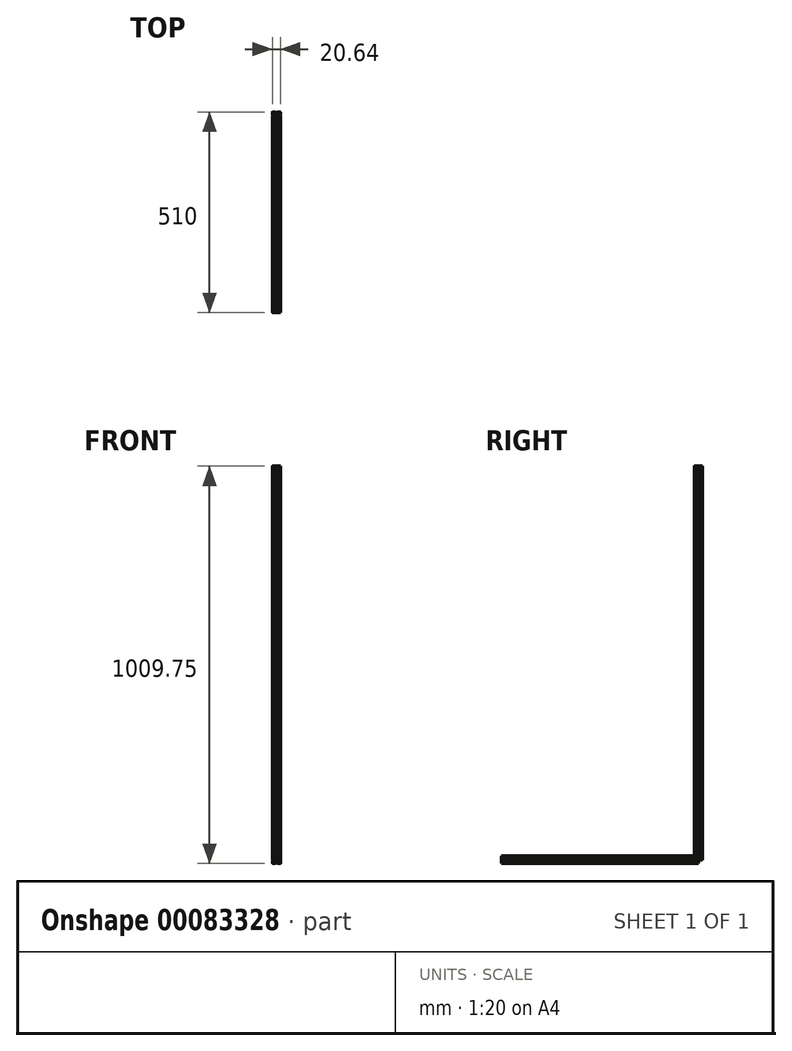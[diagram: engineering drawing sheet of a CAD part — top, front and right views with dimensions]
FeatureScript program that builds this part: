
annotation { "Feature Type Name" : "Feature", "Feature Type Description" : "" }
export const myFeature = defineFeature(function(context is Context, id is Id, definition is map)
    precondition{}
    {
        {
            assignVariable(context, id + "F0", {"name" : "VerticalLength", "anyValue" : 1000});
        }
        {
            var Q0;
            Q0=qCreatedBy(makeId("Top.planeOp"),FACE);
            var sketch = newSketch(context, id + "F1", { "sketchPlane" : qUnion([Q0])});
            skLineSegment(sketch, "E0.top", {"start": v(9.5, -10) * mm, "end": v(3.15, -10) * mm});
            skLineSegment(sketch, "E0.left", {"start": v(10, 9.5) * mm, "end": v(10, 3.15) * mm});
            skPoint(sketch, "E0.middle", {"position": v(0, 0) * mm});
            skLineSegment(sketch, "E1", {"start": v(-10, 0) * mm, "end": v(10, 0) * mm, "construction": true});
            skLineSegment(sketch, "E2", {"start": v(0, 10) * mm, "end": v(0, -10) * mm, "construction": true});
            skPoint(sketch, "E3.visualSharp", {"position": v(-10, 10) * mm});
            skPoint(sketch, "E4", {"position": v(-10, 2.65) * mm});
            skPoint(sketch, "E5.visualSharp", {"position": v(-8.5, 2.65) * mm});
            skLineSegment(sketch, "E6", {"start": v(-10, 10) * mm, "end": v(0, 0) * mm, "construction": true});
            skPoint(sketch, "E7.visualSharp", {"position": v(-8.5, 7.44) * mm});
            skLineSegment(sketch, "E8", {"start": v(-7.65, 6.59) * mm, "end": v(-3.76, 2.7) * mm});
            skLineSegment(sketch, "E9", {"start": v(-8.5, 6.23) * mm, "end": v(-8.5, 3.15) * mm});
            skLineSegment(sketch, "E10", {"start": v(-9.5, 2.65) * mm, "end": v(-9, 2.65) * mm});
            skLineSegment(sketch, "E11.bottom", {"start": v(-9.5, 10) * mm, "end": v(-3.15, 10) * mm});
            skLineSegment(sketch, "E11.top", {"start": v(-9.5, -10) * mm, "end": v(-3.15, -10) * mm});
            skLineSegment(sketch, "E11.left", {"start": v(-10, 9.5) * mm, "end": v(-10, 3.15) * mm});
            skLineSegment(sketch, "E12", {"start": v(-3.6, 2.34) * mm, "end": v(-3.6, 0) * mm});
            skLineSegment(sketch, "E13.MirrorCS", {"start": v(-2.65, 9.5) * mm, "end": v(-2.65, 9) * mm});
            skLineSegment(sketch, "E14.MirrorCS", {"start": v(-6.23, 8.5) * mm, "end": v(-3.15, 8.5) * mm});
            skLineSegment(sketch, "E15.MirrorCS", {"start": v(-2.34, 3.6) * mm, "end": v(0, 3.6) * mm});
            skLineSegment(sketch, "E16.MirrorCS", {"start": v(-6.59, 7.65) * mm, "end": v(-2.7, 3.76) * mm});
            skLineSegment(sketch, "E17.MirrorCS", {"start": v(9.5, 2.65) * mm, "end": v(9, 2.65) * mm});
            skLineSegment(sketch, "E18.MirrorCS", {"start": v(8.5, 6.23) * mm, "end": v(8.5, 3.15) * mm});
            skLineSegment(sketch, "E19.MirrorCS", {"start": v(7.65, 6.59) * mm, "end": v(3.76, 2.7) * mm});
            skLineSegment(sketch, "E20.MirrorCS", {"start": v(3.61, 2.34) * mm, "end": v(3.6, 0) * mm});
            skLineSegment(sketch, "E21.MirrorCS", {"start": v(2.34, 3.6) * mm, "end": v(0, 3.6) * mm});
            skLineSegment(sketch, "E22.MirrorCS", {"start": v(6.59, 7.65) * mm, "end": v(2.7, 3.76) * mm});
            skLineSegment(sketch, "E23.MirrorCS", {"start": v(2.65, 9.5) * mm, "end": v(2.65, 9) * mm});
            skLineSegment(sketch, "E24.MirrorCS", {"start": v(6.23, 8.5) * mm, "end": v(3.15, 8.5) * mm});
            skLineSegment(sketch, "E25.MirrorCS", {"start": v(-9.5, -2.65) * mm, "end": v(-8.8, -2.65) * mm});
            skPoint(sketch, "E26.MirrorP", {"position": v(-10, -2.65) * mm});
            skLineSegment(sketch, "E27.MirrorCS", {"start": v(2.65, -9.5) * mm, "end": v(2.65, -9) * mm});
            skLineSegment(sketch, "E28.MirrorCS", {"start": v(8.5, -6.23) * mm, "end": v(8.5, -3.15) * mm});
            skLineSegment(sketch, "E29.MirrorCS", {"start": v(3.61, -2.34) * mm, "end": v(3.6, 0) * mm});
            skLineSegment(sketch, "E30.MirrorCS", {"start": v(-3.6, -2.34) * mm, "end": v(-3.6, 0) * mm});
            skLineSegment(sketch, "E31.MirrorCS", {"start": v(-6.59, -7.65) * mm, "end": v(-2.7, -3.76) * mm});
            skLineSegment(sketch, "E32.MirrorCS", {"start": v(-2.65, -9.5) * mm, "end": v(-2.65, -9) * mm});
            skLineSegment(sketch, "E33.MirrorCS", {"start": v(-6.23, -8.5) * mm, "end": v(-3.15, -8.5) * mm});
            skPoint(sketch, "E34.MirrorP", {"position": v(-8.5, -2.65) * mm});
            skLineSegment(sketch, "E35.MirrorCS", {"start": v(7.65, -6.59) * mm, "end": v(3.76, -2.7) * mm});
            skLineSegment(sketch, "E36.MirrorCS", {"start": v(2.34, -3.6) * mm, "end": v(0, -3.6) * mm});
            skLineSegment(sketch, "E37.MirrorCS", {"start": v(6.59, -7.65) * mm, "end": v(2.7, -3.76) * mm});
            skLineSegment(sketch, "E38.MirrorCS", {"start": v(-8.5, -6.23) * mm, "end": v(-8.5, -2.95) * mm});
            skLineSegment(sketch, "E39.MirrorCS", {"start": v(-7.65, -6.59) * mm, "end": v(-3.76, -2.7) * mm});
            skLineSegment(sketch, "E40.MirrorCS", {"start": v(9.5, -2.65) * mm, "end": v(9, -2.65) * mm});
            skPoint(sketch, "E41.MirrorP", {"position": v(-8.5, -7.44) * mm});
            skPoint(sketch, "E42.MirrorP", {"position": v(-10, -10) * mm});
            skLineSegment(sketch, "E43.MirrorCS", {"start": v(6.23, -8.5) * mm, "end": v(3.15, -8.5) * mm});
            skLineSegment(sketch, "E44.MirrorCS", {"start": v(-2.34, -3.6) * mm, "end": v(0, -3.6) * mm});
            skLineSegment(sketch, "E45.trimOffspring", {"start": v(3.15, 10) * mm, "end": v(9.5, 10) * mm});
            skLineSegment(sketch, "E46.trimOffspring", {"start": v(-10, -3.15) * mm, "end": v(-10, -9.5) * mm});
            skLineSegment(sketch, "E47.trimOffspring", {"start": v(10, -3.15) * mm, "end": v(10, -9.5) * mm});
            skPoint(sketch, "E48.MirrorCS.end.orphan", {"position": v(-10, 0) * mm});
            skLineSegment(sketch, "E49.trimOffspring", {"start": v(3.15, -10) * mm, "end": v(9.5, -10) * mm});
            skLineSegment(sketch, "E50.trimOffspring", {"start": v(-3.15, -10) * mm, "end": v(-9.5, -10) * mm});
            skArc(sketch, "E51.filletArc", {"start": v(-10, 3.15) * mm, "mid": v(-9.85, 2.8) * mm, "end": v(-9.5, 2.65) * mm});
            skArc(sketch, "E52.filletArc", {"start": v(-9, 2.65) * mm, "mid": v(-8.65, 2.8) * mm, "end": v(-8.5, 3.15) * mm});
            skArc(sketch, "E53.filletArc", {"start": v(-9.5, -2.65) * mm, "mid": v(-9.85, -2.8) * mm, "end": v(-10, -3.15) * mm});
            skArc(sketch, "E54.filletArc", {"start": v(-8.5, -2.95) * mm, "mid": v(-8.59, -2.74) * mm, "end": v(-8.8, -2.65) * mm});
            skArc(sketch, "E55.filletArc", {"start": v(-9.5, 10) * mm, "mid": v(-9.85, 9.85) * mm, "end": v(-10, 9.5) * mm});
            skPoint(sketch, "E56.visualSharp", {"position": v(-2.65, 10) * mm});
            skArc(sketch, "E56.filletArc", {"start": v(-2.65, 9.5) * mm, "mid": v(-2.8, 9.85) * mm, "end": v(-3.15, 10) * mm});
            skPoint(sketch, "E57.visualSharp", {"position": v(-2.65, 8.5) * mm});
            skArc(sketch, "E57.filletArc", {"start": v(-3.15, 8.5) * mm, "mid": v(-2.8, 8.65) * mm, "end": v(-2.65, 9) * mm});
            skArc(sketch, "E58.filletArc", {"start": v(-7.65, 6.59) * mm, "mid": v(-8.2, 6.7) * mm, "end": v(-8.5, 6.23) * mm});
            skPoint(sketch, "E59.visualSharp", {"position": v(-7.44, 8.5) * mm});
            skArc(sketch, "E59.filletArc", {"start": v(-6.23, 8.5) * mm, "mid": v(-6.7, 8.2) * mm, "end": v(-6.59, 7.65) * mm});
            skPoint(sketch, "E60.visualSharp", {"position": v(-2.55, 3.6) * mm});
            skArc(sketch, "E60.filletArc", {"start": v(-2.7, 3.76) * mm, "mid": v(-2.53, 3.65) * mm, "end": v(-2.34, 3.61) * mm});
            skPoint(sketch, "E61.visualSharp", {"position": v(2.55, 3.6) * mm});
            skArc(sketch, "E61.filletArc", {"start": v(2.34, 3.6) * mm, "mid": v(2.53, 3.65) * mm, "end": v(2.7, 3.76) * mm});
            skPoint(sketch, "E62.visualSharp", {"position": v(7.44, 8.5) * mm});
            skArc(sketch, "E62.filletArc", {"start": v(6.59, 7.65) * mm, "mid": v(6.7, 8.2) * mm, "end": v(6.23, 8.5) * mm});
            skPoint(sketch, "E63.visualSharp", {"position": v(2.65, 8.5) * mm});
            skArc(sketch, "E63.filletArc", {"start": v(2.65, 9) * mm, "mid": v(2.8, 8.65) * mm, "end": v(3.15, 8.5) * mm});
            skPoint(sketch, "E64.visualSharp", {"position": v(2.65, 10) * mm});
            skArc(sketch, "E64.filletArc", {"start": v(3.15, 10) * mm, "mid": v(2.8, 9.85) * mm, "end": v(2.65, 9.5) * mm});
            skArc(sketch, "E65.filletArc", {"start": v(-10, -9.5) * mm, "mid": v(-9.85, -9.85) * mm, "end": v(-9.5, -10) * mm});
            skPoint(sketch, "E66.visualSharp", {"position": v(10, -10) * mm});
            skArc(sketch, "E66.filletArc", {"start": v(9.5, -10) * mm, "mid": v(9.85, -9.85) * mm, "end": v(10, -9.5) * mm});
            skPoint(sketch, "E67.visualSharp", {"position": v(-2.65, -8.5) * mm});
            skArc(sketch, "E67.filletArc", {"start": v(-2.65, -9) * mm, "mid": v(-2.8, -8.65) * mm, "end": v(-3.15, -8.5) * mm});
            skPoint(sketch, "E68.visualSharp", {"position": v(2.65, -8.5) * mm});
            skArc(sketch, "E68.filletArc", {"start": v(3.15, -8.5) * mm, "mid": v(2.8, -8.65) * mm, "end": v(2.65, -9) * mm});
            skPoint(sketch, "E69.visualSharp", {"position": v(-2.55, -3.61) * mm});
            skArc(sketch, "E69.filletArc", {"start": v(-2.34, -3.6) * mm, "mid": v(-2.53, -3.65) * mm, "end": v(-2.7, -3.76) * mm});
            skPoint(sketch, "E70.visualSharp", {"position": v(2.55, -3.6) * mm});
            skArc(sketch, "E70.filletArc", {"start": v(2.7, -3.76) * mm, "mid": v(2.53, -3.65) * mm, "end": v(2.34, -3.6) * mm});
            skPoint(sketch, "E71.visualSharp", {"position": v(7.44, -8.5) * mm});
            skArc(sketch, "E71.filletArc", {"start": v(6.23, -8.5) * mm, "mid": v(6.7, -8.2) * mm, "end": v(6.59, -7.65) * mm});
            skPoint(sketch, "E72.visualSharp", {"position": v(-7.44, -8.5) * mm});
            skArc(sketch, "E72.filletArc", {"start": v(-6.59, -7.65) * mm, "mid": v(-6.7, -8.2) * mm, "end": v(-6.23, -8.5) * mm});
            skArc(sketch, "E73.filletArc", {"start": v(-8.5, -6.23) * mm, "mid": v(-8.2, -6.7) * mm, "end": v(-7.65, -6.59) * mm});
            skPoint(sketch, "E74.visualSharp", {"position": v(-3.6, 2.55) * mm});
            skArc(sketch, "E74.filletArc", {"start": v(-3.6, 2.34) * mm, "mid": v(-3.65, 2.53) * mm, "end": v(-3.76, 2.7) * mm});
            skPoint(sketch, "E75.visualSharp", {"position": v(-3.6, -2.55) * mm});
            skArc(sketch, "E75.filletArc", {"start": v(-3.76, -2.7) * mm, "mid": v(-3.65, -2.53) * mm, "end": v(-3.6, -2.34) * mm});
            skPoint(sketch, "E76.visualSharp", {"position": v(3.6, 2.55) * mm});
            skArc(sketch, "E76.filletArc", {"start": v(3.76, 2.7) * mm, "mid": v(3.65, 2.53) * mm, "end": v(3.61, 2.34) * mm});
            skPoint(sketch, "E77.visualSharp", {"position": v(3.61, -2.55) * mm});
            skArc(sketch, "E77.filletArc", {"start": v(3.61, -2.34) * mm, "mid": v(3.65, -2.53) * mm, "end": v(3.76, -2.7) * mm});
            skPoint(sketch, "E78.visualSharp", {"position": v(8.5, -7.44) * mm});
            skArc(sketch, "E78.filletArc", {"start": v(7.65, -6.59) * mm, "mid": v(8.2, -6.7) * mm, "end": v(8.5, -6.23) * mm});
            skPoint(sketch, "E79.visualSharp", {"position": v(8.5, -2.65) * mm});
            skArc(sketch, "E79.filletArc", {"start": v(9, -2.65) * mm, "mid": v(8.65, -2.8) * mm, "end": v(8.5, -3.15) * mm});
            skPoint(sketch, "E80.visualSharp", {"position": v(10, -2.65) * mm});
            skArc(sketch, "E80.filletArc", {"start": v(10, -3.15) * mm, "mid": v(9.85, -2.8) * mm, "end": v(9.5, -2.65) * mm});
            skPoint(sketch, "E81.visualSharp", {"position": v(-2.65, -10) * mm});
            skArc(sketch, "E81.filletArc", {"start": v(-3.15, -10) * mm, "mid": v(-2.8, -9.85) * mm, "end": v(-2.65, -9.5) * mm});
            skPoint(sketch, "E82.visualSharp", {"position": v(2.65, -10) * mm});
            skArc(sketch, "E82.filletArc", {"start": v(2.65, -9.5) * mm, "mid": v(2.8, -9.85) * mm, "end": v(3.15, -10) * mm});
            skPoint(sketch, "E83.visualSharp", {"position": v(8.5, 7.44) * mm});
            skArc(sketch, "E83.filletArc", {"start": v(8.5, 6.23) * mm, "mid": v(8.2, 6.7) * mm, "end": v(7.65, 6.59) * mm});
            skPoint(sketch, "E84.visualSharp", {"position": v(8.5, 2.65) * mm});
            skArc(sketch, "E84.filletArc", {"start": v(8.5, 3.15) * mm, "mid": v(8.65, 2.8) * mm, "end": v(9, 2.65) * mm});
            skPoint(sketch, "E85.visualSharp", {"position": v(10, 10) * mm});
            skArc(sketch, "E85.filletArc", {"start": v(10, 9.5) * mm, "mid": v(9.85, 9.85) * mm, "end": v(9.5, 10) * mm});
            skPoint(sketch, "E86.visualSharp", {"position": v(10, 2.65) * mm});
            skArc(sketch, "E86.filletArc", {"start": v(9.5, 2.65) * mm, "mid": v(9.85, 2.8) * mm, "end": v(10, 3.15) * mm});
            skSolve(sketch);
        }
        {
            var Q0;
            Q0=makeQuery(id+"F1.imprint","IMPRINT",FACE,{"disambiguationData":[TD([[makeQuery(id+"F1.imprint","IMPRINT",EDGE,{"derivedFrom":sQuery(id+"F1.wireOp",EDGE,"E8")}),1.0]])]});
            extrude(context, id + "F2", {"entities" : qUnion([Q0]), "depth" : (getVariable(context, 'VerticalLength')) * mm});
        }
        {
            assignVariable(context, id + "F3", {"name" : "HorizontalLength", "anyValue" : 500});
        }
        {
            var Q0;
            Q0=qCreatedBy(makeId("Front.planeOp"),FACE);
            var sketch = newSketch(context, id + "F4", { "sketchPlane" : qUnion([Q0])});
            skLineSegment(sketch, "E87.top", {"start": v(10.14, -9.75) * mm, "end": v(3.8, -9.75) * mm});
            skLineSegment(sketch, "E87.left", {"start": v(10.64, 9.75) * mm, "end": v(10.64, 3.4) * mm});
            skPoint(sketch, "E87.middle", {"position": v(0.64, 0.25) * mm});
            skLineSegment(sketch, "E88", {"start": v(-9.36, 0.25) * mm, "end": v(10.64, 0.25) * mm, "construction": true});
            skLineSegment(sketch, "E89", {"start": v(0.64, 10.25) * mm, "end": v(0.64, -9.75) * mm, "construction": true});
            skPoint(sketch, "E90.visualSharp", {"position": v(-9.36, 10.25) * mm});
            skPoint(sketch, "E91", {"position": v(-9.36, 2.9) * mm});
            skPoint(sketch, "E92.visualSharp", {"position": v(-7.86, 2.9) * mm});
            skLineSegment(sketch, "E93", {"start": v(-9.36, 10.25) * mm, "end": v(0.64, 0.25) * mm, "construction": true});
            skPoint(sketch, "E94.visualSharp", {"position": v(-7.86, 7.7) * mm});
            skLineSegment(sketch, "E95", {"start": v(-7, 6.84) * mm, "end": v(-3.11, 2.95) * mm});
            skLineSegment(sketch, "E96", {"start": v(-7.86, 6.48) * mm, "end": v(-7.86, 3.4) * mm});
            skLineSegment(sketch, "E97", {"start": v(-8.86, 2.9) * mm, "end": v(-8.36, 2.9) * mm});
            skLineSegment(sketch, "E98.bottom", {"start": v(-8.86, 10.25) * mm, "end": v(-2.5, 10.25) * mm});
            skLineSegment(sketch, "E98.top", {"start": v(-8.86, -9.75) * mm, "end": v(-2.5, -9.75) * mm});
            skLineSegment(sketch, "E98.left", {"start": v(-9.36, 9.75) * mm, "end": v(-9.36, 3.4) * mm});
            skLineSegment(sketch, "E99", {"start": v(-2.97, 2.6) * mm, "end": v(-2.97, 0.25) * mm});
            skLineSegment(sketch, "E100.MirrorCS", {"start": v(-2, 9.75) * mm, "end": v(-2, 9.25) * mm});
            skLineSegment(sketch, "E101.MirrorCS", {"start": v(-5.59, 8.75) * mm, "end": v(-2.5, 8.75) * mm});
            skLineSegment(sketch, "E102.MirrorCS", {"start": v(-1.7, 3.86) * mm, "end": v(0.64, 3.86) * mm});
            skLineSegment(sketch, "E103.MirrorCS", {"start": v(-5.94, 7.9) * mm, "end": v(-2.05, 4) * mm});
            skLineSegment(sketch, "E104.MirrorCS", {"start": v(10.14, 2.9) * mm, "end": v(9.64, 2.9) * mm});
            skLineSegment(sketch, "E105.MirrorCS", {"start": v(9.14, 6.48) * mm, "end": v(9.14, 3.4) * mm});
            skLineSegment(sketch, "E106.MirrorCS", {"start": v(8.3, 6.84) * mm, "end": v(4.4, 2.95) * mm});
            skLineSegment(sketch, "E107.MirrorCS", {"start": v(4.25, 2.6) * mm, "end": v(4.25, 0.25) * mm});
            skLineSegment(sketch, "E108.MirrorCS", {"start": v(2.99, 3.86) * mm, "end": v(0.64, 3.86) * mm});
            skLineSegment(sketch, "E109.MirrorCS", {"start": v(7.23, 7.9) * mm, "end": v(3.34, 4) * mm});
            skLineSegment(sketch, "E110.MirrorCS", {"start": v(3.3, 9.75) * mm, "end": v(3.3, 9.25) * mm});
            skLineSegment(sketch, "E111.MirrorCS", {"start": v(6.88, 8.75) * mm, "end": v(3.8, 8.75) * mm});
            skLineSegment(sketch, "E112.MirrorCS", {"start": v(-8.86, -2.4) * mm, "end": v(-8.16, -2.4) * mm});
            skPoint(sketch, "E113.MirrorP", {"position": v(-9.36, -2.4) * mm});
            skLineSegment(sketch, "E114.MirrorCS", {"start": v(3.3, -9.25) * mm, "end": v(3.3, -8.75) * mm});
            skLineSegment(sketch, "E115.MirrorCS", {"start": v(9.14, -5.98) * mm, "end": v(9.14, -2.9) * mm});
            skLineSegment(sketch, "E116.MirrorCS", {"start": v(4.25, -2.09) * mm, "end": v(4.25, 0.25) * mm});
            skLineSegment(sketch, "E117.MirrorCS", {"start": v(-2.97, -2.09) * mm, "end": v(-2.97, 0.25) * mm});
            skLineSegment(sketch, "E118.MirrorCS", {"start": v(-5.94, -7.4) * mm, "end": v(-2.05, -3.5) * mm});
            skLineSegment(sketch, "E119.MirrorCS", {"start": v(-2, -9.25) * mm, "end": v(-2, -8.75) * mm});
            skLineSegment(sketch, "E120.MirrorCS", {"start": v(-5.59, -8.25) * mm, "end": v(-2.5, -8.25) * mm});
            skPoint(sketch, "E121.MirrorP", {"position": v(-7.86, -2.4) * mm});
            skLineSegment(sketch, "E122.MirrorCS", {"start": v(8.3, -6.33) * mm, "end": v(4.4, -2.44) * mm});
            skLineSegment(sketch, "E123.MirrorCS", {"start": v(2.99, -3.36) * mm, "end": v(0.64, -3.36) * mm});
            skLineSegment(sketch, "E124.MirrorCS", {"start": v(7.23, -7.4) * mm, "end": v(3.34, -3.5) * mm});
            skLineSegment(sketch, "E125.MirrorCS", {"start": v(-7.86, -5.98) * mm, "end": v(-7.86, -2.7) * mm});
            skLineSegment(sketch, "E126.MirrorCS", {"start": v(-7, -6.33) * mm, "end": v(-3.11, -2.44) * mm});
            skLineSegment(sketch, "E127.MirrorCS", {"start": v(10.14, -2.4) * mm, "end": v(9.64, -2.4) * mm});
            skPoint(sketch, "E128.MirrorP", {"position": v(-7.86, -7.19) * mm});
            skPoint(sketch, "E129.MirrorP", {"position": v(-9.36, -9.75) * mm});
            skLineSegment(sketch, "E130.MirrorCS", {"start": v(6.88, -8.25) * mm, "end": v(3.8, -8.25) * mm});
            skLineSegment(sketch, "E131.MirrorCS", {"start": v(-1.7, -3.36) * mm, "end": v(0.64, -3.36) * mm});
            skLineSegment(sketch, "E132.trimOffspring", {"start": v(3.8, 10.25) * mm, "end": v(10.14, 10.25) * mm});
            skLineSegment(sketch, "E133.trimOffspring", {"start": v(-9.36, -2.9) * mm, "end": v(-9.36, -9.25) * mm});
            skLineSegment(sketch, "E134.trimOffspring", {"start": v(10.64, -2.9) * mm, "end": v(10.64, -9.25) * mm});
            skPoint(sketch, "E135.MirrorCS.end.orphan", {"position": v(-9.36, 0.25) * mm});
            skLineSegment(sketch, "E136.trimOffspring", {"start": v(3.8, -9.75) * mm, "end": v(10.14, -9.75) * mm});
            skLineSegment(sketch, "E137.trimOffspring", {"start": v(-2.5, -9.75) * mm, "end": v(-8.86, -9.75) * mm});
            skArc(sketch, "E138.filletArc", {"start": v(-9.36, 3.4) * mm, "mid": v(-9.2, 3.05) * mm, "end": v(-8.86, 2.9) * mm});
            skArc(sketch, "E139.filletArc", {"start": v(-8.36, 2.9) * mm, "mid": v(-8, 3.05) * mm, "end": v(-7.86, 3.4) * mm});
            skArc(sketch, "E140.filletArc", {"start": v(-8.86, -2.4) * mm, "mid": v(-9.2, -2.54) * mm, "end": v(-9.36, -2.9) * mm});
            skArc(sketch, "E141.filletArc", {"start": v(-7.86, -2.7) * mm, "mid": v(-7.94, -2.49) * mm, "end": v(-8.16, -2.4) * mm});
            skArc(sketch, "E142.filletArc", {"start": v(-8.86, 10.25) * mm, "mid": v(-9.2, 10.1) * mm, "end": v(-9.36, 9.75) * mm});
            skPoint(sketch, "E143.visualSharp", {"position": v(-2, 10.25) * mm});
            skArc(sketch, "E143.filletArc", {"start": v(-2, 9.75) * mm, "mid": v(-2.15, 10.1) * mm, "end": v(-2.5, 10.25) * mm});
            skPoint(sketch, "E144.visualSharp", {"position": v(-2, 8.75) * mm});
            skArc(sketch, "E144.filletArc", {"start": v(-2.5, 8.75) * mm, "mid": v(-2.15, 8.9) * mm, "end": v(-2, 9.25) * mm});
            skArc(sketch, "E145.filletArc", {"start": v(-7, 6.84) * mm, "mid": v(-7.55, 6.95) * mm, "end": v(-7.86, 6.48) * mm});
            skPoint(sketch, "E146.visualSharp", {"position": v(-6.8, 8.75) * mm});
            skArc(sketch, "E146.filletArc", {"start": v(-5.59, 8.75) * mm, "mid": v(-6.05, 8.44) * mm, "end": v(-5.94, 7.9) * mm});
            skPoint(sketch, "E147.visualSharp", {"position": v(-1.9, 3.86) * mm});
            skArc(sketch, "E147.filletArc", {"start": v(-2.05, 4) * mm, "mid": v(-1.89, 3.9) * mm, "end": v(-1.7, 3.86) * mm});
            skPoint(sketch, "E148.visualSharp", {"position": v(3.2, 3.86) * mm});
            skArc(sketch, "E148.filletArc", {"start": v(2.99, 3.86) * mm, "mid": v(3.18, 3.9) * mm, "end": v(3.34, 4) * mm});
            skPoint(sketch, "E149.visualSharp", {"position": v(8.08, 8.75) * mm});
            skArc(sketch, "E149.filletArc", {"start": v(7.23, 7.9) * mm, "mid": v(7.34, 8.44) * mm, "end": v(6.88, 8.75) * mm});
            skPoint(sketch, "E150.visualSharp", {"position": v(3.3, 8.75) * mm});
            skArc(sketch, "E150.filletArc", {"start": v(3.3, 9.25) * mm, "mid": v(3.44, 8.9) * mm, "end": v(3.8, 8.75) * mm});
            skPoint(sketch, "E151.visualSharp", {"position": v(3.3, 10.25) * mm});
            skArc(sketch, "E151.filletArc", {"start": v(3.8, 10.25) * mm, "mid": v(3.44, 10.1) * mm, "end": v(3.3, 9.75) * mm});
            skArc(sketch, "E152.filletArc", {"start": v(-9.36, -9.25) * mm, "mid": v(-9.2, -9.6) * mm, "end": v(-8.86, -9.75) * mm});
            skPoint(sketch, "E153.visualSharp", {"position": v(10.64, -9.75) * mm});
            skArc(sketch, "E153.filletArc", {"start": v(10.14, -9.75) * mm, "mid": v(10.5, -9.6) * mm, "end": v(10.64, -9.25) * mm});
            skPoint(sketch, "E154.visualSharp", {"position": v(-2, -8.25) * mm});
            skArc(sketch, "E154.filletArc", {"start": v(-2, -8.75) * mm, "mid": v(-2.15, -8.4) * mm, "end": v(-2.5, -8.25) * mm});
            skPoint(sketch, "E155.visualSharp", {"position": v(3.3, -8.25) * mm});
            skArc(sketch, "E155.filletArc", {"start": v(3.8, -8.25) * mm, "mid": v(3.44, -8.4) * mm, "end": v(3.3, -8.75) * mm});
            skPoint(sketch, "E156.visualSharp", {"position": v(-1.9, -3.36) * mm});
            skArc(sketch, "E156.filletArc", {"start": v(-1.7, -3.36) * mm, "mid": v(-1.89, -3.4) * mm, "end": v(-2.05, -3.5) * mm});
            skPoint(sketch, "E157.visualSharp", {"position": v(3.2, -3.36) * mm});
            skArc(sketch, "E157.filletArc", {"start": v(3.34, -3.5) * mm, "mid": v(3.18, -3.4) * mm, "end": v(2.99, -3.36) * mm});
            skPoint(sketch, "E158.visualSharp", {"position": v(8.08, -8.25) * mm});
            skArc(sketch, "E158.filletArc", {"start": v(6.88, -8.25) * mm, "mid": v(7.34, -7.94) * mm, "end": v(7.23, -7.4) * mm});
            skPoint(sketch, "E159.visualSharp", {"position": v(-6.8, -8.25) * mm});
            skArc(sketch, "E159.filletArc", {"start": v(-5.94, -7.4) * mm, "mid": v(-6.05, -7.94) * mm, "end": v(-5.59, -8.25) * mm});
            skArc(sketch, "E160.filletArc", {"start": v(-7.86, -5.98) * mm, "mid": v(-7.55, -6.44) * mm, "end": v(-7, -6.33) * mm});
            skPoint(sketch, "E161.visualSharp", {"position": v(-2.97, 2.8) * mm});
            skArc(sketch, "E161.filletArc", {"start": v(-2.97, 2.6) * mm, "mid": v(-3, 2.79) * mm, "end": v(-3.11, 2.95) * mm});
            skPoint(sketch, "E162.visualSharp", {"position": v(-2.97, -2.3) * mm});
            skArc(sketch, "E162.filletArc", {"start": v(-3.11, -2.44) * mm, "mid": v(-3, -2.28) * mm, "end": v(-2.97, -2.09) * mm});
            skPoint(sketch, "E163.visualSharp", {"position": v(4.25, 2.8) * mm});
            skArc(sketch, "E163.filletArc", {"start": v(4.4, 2.95) * mm, "mid": v(4.3, 2.79) * mm, "end": v(4.25, 2.6) * mm});
            skPoint(sketch, "E164.visualSharp", {"position": v(4.25, -2.3) * mm});
            skArc(sketch, "E164.filletArc", {"start": v(4.25, -2.09) * mm, "mid": v(4.3, -2.28) * mm, "end": v(4.4, -2.44) * mm});
            skPoint(sketch, "E165.visualSharp", {"position": v(9.14, -7.19) * mm});
            skArc(sketch, "E165.filletArc", {"start": v(8.3, -6.33) * mm, "mid": v(8.84, -6.44) * mm, "end": v(9.14, -5.98) * mm});
            skPoint(sketch, "E166.visualSharp", {"position": v(9.14, -2.4) * mm});
            skArc(sketch, "E166.filletArc", {"start": v(9.64, -2.4) * mm, "mid": v(9.3, -2.54) * mm, "end": v(9.14, -2.9) * mm});
            skPoint(sketch, "E167.visualSharp", {"position": v(10.64, -2.4) * mm});
            skArc(sketch, "E167.filletArc", {"start": v(10.64, -2.9) * mm, "mid": v(10.5, -2.54) * mm, "end": v(10.14, -2.4) * mm});
            skPoint(sketch, "E168.visualSharp", {"position": v(-2, -9.75) * mm});
            skArc(sketch, "E168.filletArc", {"start": v(-2.5, -9.75) * mm, "mid": v(-2.15, -9.6) * mm, "end": v(-2, -9.25) * mm});
            skPoint(sketch, "E169.visualSharp", {"position": v(3.3, -9.75) * mm});
            skArc(sketch, "E169.filletArc", {"start": v(3.3, -9.25) * mm, "mid": v(3.44, -9.6) * mm, "end": v(3.8, -9.75) * mm});
            skPoint(sketch, "E170.visualSharp", {"position": v(9.14, 7.7) * mm});
            skArc(sketch, "E170.filletArc", {"start": v(9.14, 6.48) * mm, "mid": v(8.84, 6.95) * mm, "end": v(8.3, 6.84) * mm});
            skPoint(sketch, "E171.visualSharp", {"position": v(9.14, 2.9) * mm});
            skArc(sketch, "E171.filletArc", {"start": v(9.14, 3.4) * mm, "mid": v(9.3, 3.05) * mm, "end": v(9.64, 2.9) * mm});
            skPoint(sketch, "E172.visualSharp", {"position": v(10.64, 10.25) * mm});
            skArc(sketch, "E172.filletArc", {"start": v(10.64, 9.75) * mm, "mid": v(10.5, 10.1) * mm, "end": v(10.14, 10.25) * mm});
            skPoint(sketch, "E173.visualSharp", {"position": v(10.64, 2.9) * mm});
            skArc(sketch, "E173.filletArc", {"start": v(10.14, 2.9) * mm, "mid": v(10.5, 3.05) * mm, "end": v(10.64, 3.4) * mm});
            skSolve(sketch);
        }
        {
            var Q0;
            Q0=makeQuery(id+"F4.imprint","IMPRINT",FACE,{"disambiguationData":[TD([[makeQuery(id+"F4.imprint","IMPRINT",EDGE,{"derivedFrom":sQuery(id+"F4.wireOp",EDGE,"E95")}),1.0]])]});
            extrude(context, id + "F5", {"entities" : qUnion([Q0]), "depth" : (getVariable(context, 'HorizontalLength')) * mm});
        }
    });
